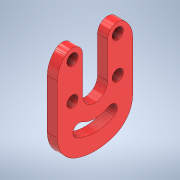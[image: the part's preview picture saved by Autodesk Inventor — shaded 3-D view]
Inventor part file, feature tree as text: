
AUTODESK INVENTOR PART (.ipt)
format: ipt  version: 2021 (Build 250183000, 183)  size: 150,016 bytes
history: native  units: in
note: dims shown in document units (in); Inventor stores cm internally (conversion verified against a paired STEP export)
features: extrude x1, sketch x1
ambient origin geometry x8: Origin, YZ Plane, XZ Plane, XY Plane, X Axis, Y Axis, Z Axis, Center Point
bodies: Solid1 (feature_tree)
feature tree (2):
  extrude  "Extrusion1"  Depth=0.9843in
  sketch  "Sketch1"  dims[d12=0.7874in d19=0.9843in d21=0.4331in d22=0.4331in d23=0.4331in d24=1.4173in d25=1.2598in d26=0.2362in d27=0.3937in d28=0.0in]
